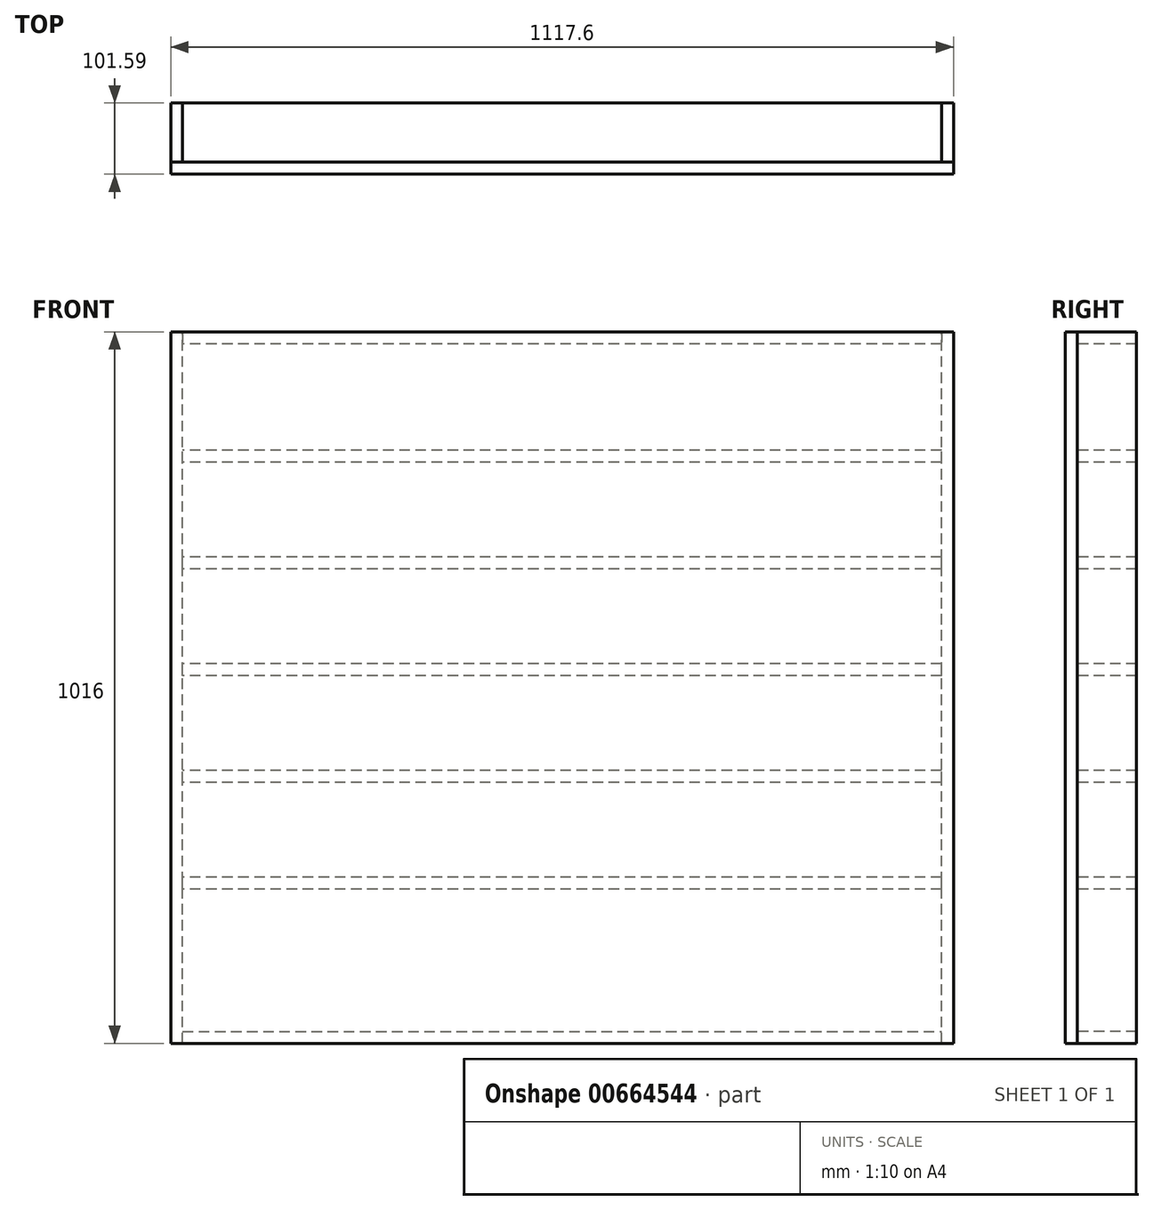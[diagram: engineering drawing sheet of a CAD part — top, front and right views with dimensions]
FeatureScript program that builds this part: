
annotation { "Feature Type Name" : "Feature", "Feature Type Description" : "" }
export const myFeature = defineFeature(function(context is Context, id is Id, definition is map)
    precondition{}
    {
        {
            var Q0;
            Q0=qCreatedBy(makeId("Front.planeOp"),FACE);
            var sketch = newSketch(context, id + "F0", { "sketchPlane" : qUnion([Q0])});
            skLineSegment(sketch, "E0.bottom", {"start": v(0, 0) * mm, "end": v(1117.6, 0) * mm});
            skLineSegment(sketch, "E0.top", {"start": v(0, 1016) * mm, "end": v(1117.6, 1016) * mm});
            skLineSegment(sketch, "E0.left", {"start": v(0, 0) * mm, "end": v(0, 1016) * mm});
            skLineSegment(sketch, "E0.right", {"start": v(1117.6, 0) * mm, "end": v(1117.6, 1016) * mm});
            skSolve(sketch);
        }
        {
            var Q0;
            Q0 = qSketchRegion(id + "F0", true);
            extrude(context, id + "F1", {"entities" : qUnion([Q0]), "depth" : 17.14 * mm, "offsetDistance" : 25.4 * mm});
        }
        {
            var Q0;
            Q0=makeQuery(id+"F1.opExtrude","CAP_FACE",FACE,{"disambiguationData":[OSD([sQuery(id+"F0.wireOp",EDGE,"E0.bottom"),sQuery(id+"F0.wireOp",EDGE,"E0.top"),sQuery(id+"F0.wireOp",EDGE,"E0.left"),sQuery(id+"F0.wireOp",EDGE,"E0.right")])],"isStart":true});
            var sketch = newSketch(context, id + "F2", { "sketchPlane" : qUnion([Q0])});
            skLineSegment(sketch, "E1.bottom", {"start": v(0, 0) * mm, "end": v(-17.15, 0) * mm});
            skLineSegment(sketch, "E1.top", {"start": v(0, 1016) * mm, "end": v(-17.15, 1016) * mm});
            skLineSegment(sketch, "E1.left", {"start": v(0, 0) * mm, "end": v(0, 1016) * mm});
            skLineSegment(sketch, "E1.right", {"start": v(-17.15, 0) * mm, "end": v(-17.15, 1016) * mm});
            skSolve(sketch);
        }
        {
            var Q0;
            Q0 = qSketchRegion(id + "F2", true);
            extrude(context, id + "F3", {"entities" : qUnion([Q0]), "depth" : 84.45 * mm, "offsetDistance" : 25.4 * mm});
        }
        {
            var Q0;
            Q0=makeQuery(id+"F1.opExtrude","CAP_FACE",FACE,{"disambiguationData":[OSD([sQuery(id+"F0.wireOp",EDGE,"E0.bottom"),sQuery(id+"F0.wireOp",EDGE,"E0.top"),sQuery(id+"F0.wireOp",EDGE,"E0.left"),sQuery(id+"F0.wireOp",EDGE,"E0.right")])],"isStart":true});
            var sketch = newSketch(context, id + "F4", { "sketchPlane" : qUnion([Q0])});
            skLineSegment(sketch, "E2.bottom", {"start": v(-1117.6, 0) * mm, "end": v(-1100.46, 0) * mm});
            skLineSegment(sketch, "E2.top", {"start": v(-1117.6, 1016) * mm, "end": v(-1100.46, 1016) * mm});
            skLineSegment(sketch, "E2.left", {"start": v(-1117.6, 0) * mm, "end": v(-1117.6, 1016) * mm});
            skLineSegment(sketch, "E2.right", {"start": v(-1100.46, 0) * mm, "end": v(-1100.46, 1016) * mm});
            skSolve(sketch);
        }
        {
            var Q0;
            Q0 = qSketchRegion(id + "F4", true);
            extrude(context, id + "F5", {"entities" : qUnion([Q0]), "depth" : 84.45 * mm, "offsetDistance" : 25.4 * mm});
        }
        {
            var Q0;
            Q0=makeQuery(id+"F1.opExtrude","CAP_FACE",FACE,{"disambiguationData":[OSD([sQuery(id+"F0.wireOp",EDGE,"E0.bottom"),sQuery(id+"F0.wireOp",EDGE,"E0.top"),sQuery(id+"F0.wireOp",EDGE,"E0.left"),sQuery(id+"F0.wireOp",EDGE,"E0.right")])],"isStart":true});
            var sketch = newSketch(context, id + "F6", { "sketchPlane" : qUnion([Q0])});
            skLineSegment(sketch, "E3.bottom", {"start": v(-1100.46, 1016) * mm, "end": v(-17.15, 1016) * mm});
            skLineSegment(sketch, "E3.top", {"start": v(-1100.46, 998.85) * mm, "end": v(-17.15, 998.85) * mm});
            skLineSegment(sketch, "E3.left", {"start": v(-1100.46, 1016) * mm, "end": v(-1100.46, 998.85) * mm});
            skLineSegment(sketch, "E3.right", {"start": v(-17.15, 1016) * mm, "end": v(-17.15, 998.85) * mm});
            skLineSegment(sketch, "E4.bottom", {"start": v(-17.14, 0) * mm, "end": v(-1100.46, 0) * mm});
            skLineSegment(sketch, "E4.top", {"start": v(-17.14, 17.15) * mm, "end": v(-1100.46, 17.14) * mm});
            skLineSegment(sketch, "E4.left", {"start": v(-17.15, 0) * mm, "end": v(-17.15, 17.15) * mm});
            skLineSegment(sketch, "E4.right", {"start": v(-1100.46, 0) * mm, "end": v(-1100.46, 17.14) * mm});
            skSolve(sketch);
        }
        {
            var Q0;
            Q0 = qSketchRegion(id + "F6", true);
            extrude(context, id + "F7", {"entities" : qUnion([Q0]), "depth" : 84.45 * mm, "offsetDistance" : 25.4 * mm});
        }
        {
            var Q0;
            Q0=makeQuery(id+"F1.opExtrude","CAP_FACE",FACE,{"disambiguationData":[OSD([sQuery(id+"F0.wireOp",EDGE,"E0.bottom"),sQuery(id+"F0.wireOp",EDGE,"E0.top"),sQuery(id+"F0.wireOp",EDGE,"E0.left"),sQuery(id+"F0.wireOp",EDGE,"E0.right")])],"isStart":true});
            var sketch = newSketch(context, id + "F8", { "sketchPlane" : qUnion([Q0])});
            skLineSegment(sketch, "E5.bottom", {"start": v(-1100.46, 220.35) * mm, "end": v(-17.15, 220.35) * mm});
            skLineSegment(sketch, "E5.top", {"start": v(-1100.46, 237.5) * mm, "end": v(-17.15, 237.5) * mm});
            skLineSegment(sketch, "E5.left", {"start": v(-1100.46, 220.35) * mm, "end": v(-1100.46, 237.5) * mm});
            skLineSegment(sketch, "E5.right", {"start": v(-17.15, 220.35) * mm, "end": v(-17.15, 237.5) * mm});
            skLineSegment(sketch, "E6.0.1.0", {"start": v(-1100.46, 372.75) * mm, "end": v(-17.15, 372.75) * mm});
            skLineSegment(sketch, "E6.0.1.1", {"start": v(-1100.46, 389.9) * mm, "end": v(-17.15, 389.9) * mm});
            skLineSegment(sketch, "E6.0.1.2", {"start": v(-1100.46, 372.75) * mm, "end": v(-1100.46, 389.9) * mm});
            skLineSegment(sketch, "E6.0.1.3", {"start": v(-17.15, 372.75) * mm, "end": v(-17.15, 389.9) * mm});
            skLineSegment(sketch, "E6.0.2.0", {"start": v(-1100.46, 525.15) * mm, "end": v(-17.15, 525.15) * mm});
            skLineSegment(sketch, "E6.0.2.1", {"start": v(-1100.46, 542.3) * mm, "end": v(-17.15, 542.3) * mm});
            skLineSegment(sketch, "E6.0.2.2", {"start": v(-1100.46, 525.15) * mm, "end": v(-1100.46, 542.3) * mm});
            skLineSegment(sketch, "E6.0.2.3", {"start": v(-17.15, 525.15) * mm, "end": v(-17.15, 542.3) * mm});
            skLineSegment(sketch, "E6.0.3.0", {"start": v(-1100.46, 677.55) * mm, "end": v(-17.15, 677.55) * mm});
            skLineSegment(sketch, "E6.0.3.1", {"start": v(-1100.46, 694.7) * mm, "end": v(-17.15, 694.7) * mm});
            skLineSegment(sketch, "E6.0.3.2", {"start": v(-1100.46, 677.55) * mm, "end": v(-1100.46, 694.7) * mm});
            skLineSegment(sketch, "E6.0.3.3", {"start": v(-17.15, 677.55) * mm, "end": v(-17.15, 694.7) * mm});
            skLineSegment(sketch, "E6.0.4.0", {"start": v(-1100.46, 829.95) * mm, "end": v(-17.15, 829.95) * mm});
            skLineSegment(sketch, "E6.0.4.1", {"start": v(-1100.46, 847.1) * mm, "end": v(-17.15, 847.1) * mm});
            skLineSegment(sketch, "E6.0.4.2", {"start": v(-1100.46, 829.95) * mm, "end": v(-1100.46, 847.1) * mm});
            skLineSegment(sketch, "E6.0.4.3", {"start": v(-17.15, 829.95) * mm, "end": v(-17.15, 847.1) * mm});
            skLineSegment(sketch, "E6.direction1", {"start": v(-1100.46, 169.54) * mm, "end": v(-1075.06, 169.54) * mm, "construction": true});
            skLineSegment(sketch, "E6.direction2", {"start": v(-1100.46, 169.54) * mm, "end": v(-1100.46, 321.95) * mm, "construction": true});
            skSolve(sketch);
        }
        {
            var Q0;
            Q0 = qSketchRegion(id + "F8", true);
            extrude(context, id + "F9", {"entities" : qUnion([Q0]), "depth" : 84.45 * mm, "offsetDistance" : 25.4 * mm});
        }
    });
